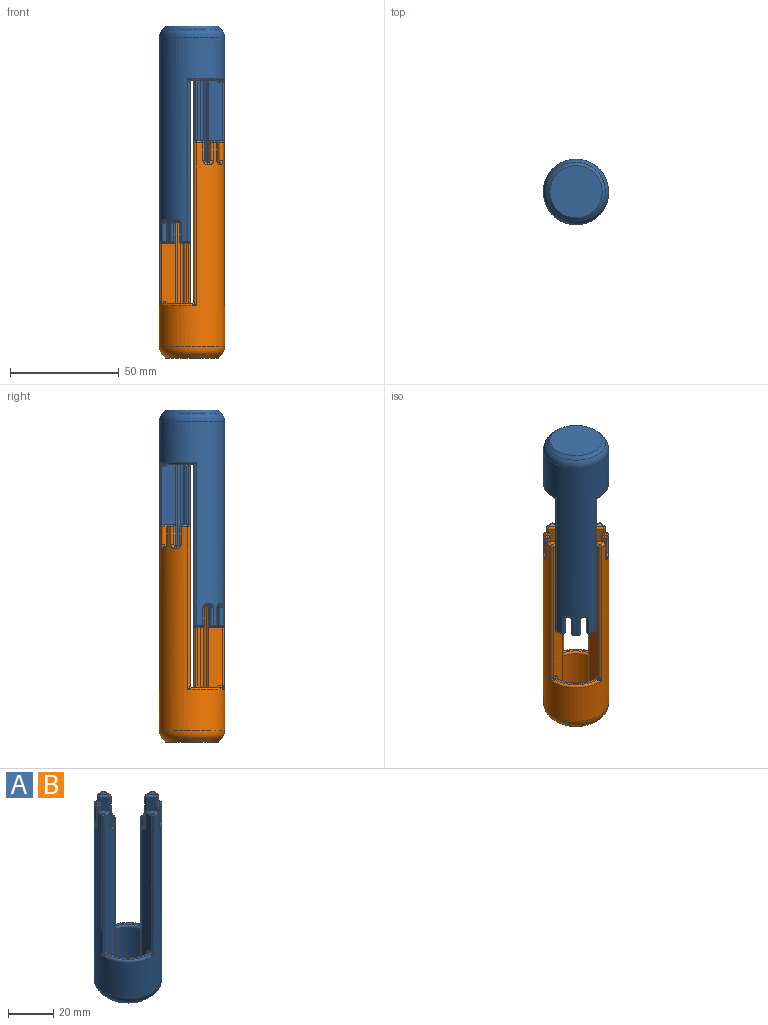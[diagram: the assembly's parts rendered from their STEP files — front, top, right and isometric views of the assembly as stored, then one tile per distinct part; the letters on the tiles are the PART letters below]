
ASSEMBLY  parts=2 mates=1
PART A: 263 faces, bbox 32.5x32.5x100 mm
  f0: cone r=12.88mm half-angle=45deg, axis (0,0,1), area 17.4mm2, adj f4,f217,f223,f235,f236,f237
  f1: cylinder r=12mm len=94mm, axis (0,0,1), area 703.3mm2, adj f26,f27,f166,f168,f170,f172,f176,f180
  f2: cylinder r=12mm len=19.76mm, axis (0,0,1), area 361.6mm2, adj f5,f228,f232,f234
  f3: plane 19.7x19.7mm, normal (0,0,1), area 194.3mm2, adj f235,f236,f237,f238,f239,f240,f241,f242
  f4: cylinder r=12mm len=19.76mm, axis (0,0,1), area 361.6mm2, adj f0,f217,f221,f223
  f5: cone r=12.88mm half-angle=45deg, axis (0,0,1), area 17.4mm2, adj f2,f228,f234,f260,f261,f262
  f6: cylinder r=12mm len=94mm, axis (0,0,1), area 703.3mm2, adj f28,f29,f103,f105,f107,f109,f113,f117
  f7: plane 1.63x1.25mm, normal (0,0,1), area 1mm2, adj f80,f84,f105,f112
  f8: plane 0.66x0.66mm, normal (0,0,1), area 0.2mm2, adj f73,f138,f142
  f9: plane 0.66x0.66mm, normal (0,0,1), area 0.2mm2, adj f67,f151,f152
  f10: plane 1.63x1.25mm, normal (0,0,1), area 1mm2, adj f57,f58,f184,f193
  f11: cylinder r=15mm len=93.93mm, axis (0,0,-1), area 4539.2mm2, adj f37,f38,f39,f40,f41,f42,f44,f104
  f12: plane 3.66x2.95mm, normal (0,0,1), area 5.6mm2, adj f63,f202,f206
  f13: plane 2.12x2.12mm, normal (0,0,1), area 2mm2, adj f62,f70,f176,f185
  f14: plane 3.66x2.95mm, normal (0,0,1), area 5.6mm2, adj f71,f136,f141
  f15: plane 2.12x2.12mm, normal (0,0,1), area 2mm2, adj f72,f78,f113,f120
  f16: plane 94x6.14mm, normal (0,-1,0), area 493.6mm2, adj f37,f206,f208,f211,f212,f216,f217,f219
  f17: plane 94x6.14mm, normal (-1,0,0), area 493.6mm2, adj f38,f141,f144,f146,f148,f220,f222,f223
  f18: plane 84.01x1mm, normal (0,-1,0), area 84mm2, adj f149,f152,f154,f155,f256
  f19: plane 84.31x2.17mm, normal (-1,0,0), area 182.6mm2, adj f26,f149,f151,f153,f252
  f20: plane 84.31x2.17mm, normal (0,1,0), area 182.6mm2, adj f27,f198,f200,f201,f244
  f21: plane 84.01x1mm, normal (1,0,0), area 84mm2, adj f201,f205,f207,f208,f240
  f22: plane 84.01x1mm, normal (0,1,0), area 84mm2, adj f137,f142,f144,f145,f241
  f23: plane 84.31x2.17mm, normal (1,0,0), area 182.6mm2, adj f28,f135,f137,f138,f245
  f24: plane 84.31x2.17mm, normal (0,-1,0), area 182.6mm2, adj f29,f85,f88,f91,f253
  f25: plane 84.01x1mm, normal (-1,0,0), area 84mm2, adj f85,f87,f89,f90,f257
  f26: cylinder r=1mm len=84.59mm, axis (0,0,1), area 170.4mm2, adj f1,f19,f156,f158,f160,f164,f250
  f27: cylinder r=1mm len=84.59mm, axis (0,0,1), area 170.4mm2, adj f1,f20,f188,f192,f194,f196,f246
  f28: cylinder r=1mm len=84.59mm, axis (0,0,1), area 170.4mm2, adj f6,f23,f125,f129,f131,f133,f247
  f29: cylinder r=1mm len=84.59mm, axis (0,0,1), area 170.4mm2, adj f6,f24,f93,f95,f97,f101,f251
  f30: plane 13.75x13.75mm, normal (0,0,1), area 20.7mm2, adj f39,f214,f216,f218,f220,f221
  f31: plane 3.66x2.95mm, normal (0,0,1), area 5.6mm2, adj f69,f165,f169
  f32: plane 3.66x2.95mm, normal (0,0,1), area 5.6mm2, adj f79,f100,f104
  f33: plane 24x24mm, normal (0,0,-1), area 452.4mm2, adj f43
  f34: plane 13.75x13.75mm, normal (0,0,1), area 20.7mm2, adj f42,f225,f227,f229,f231,f232
  f35: plane 94x6.14mm, normal (1,0,0), area 493.6mm2, adj f41,f154,f159,f161,f165,f231,f233,f234
  f36: plane 94x6.14mm, normal (0,1,0), area 493.6mm2, adj f40,f90,f94,f96,f100,f227,f228,f230
  f37: cylinder r=1mm len=75mm, axis (0,0,-1), area 125mm2, adj f11,f16,f204,f213,f214
  f38: cylinder r=1mm len=75mm, axis (0,0,-1), area 125mm2, adj f11,f17,f139,f215,f218
  f39: torus R=14mm, axis (0,0,1), area 38.6mm2, adj f11,f30,f213,f215
  f40: cylinder r=1mm len=75mm, axis (0,0,-1), area 125mm2, adj f11,f36,f102,f224,f225
  f41: cylinder r=1mm len=75mm, axis (0,0,-1), area 125mm2, adj f11,f35,f167,f226,f229
  f42: torus R=14mm, axis (0,0,1), area 38.6mm2, adj f11,f34,f224,f226
  f43: cone r=15mm half-angle=45deg, axis (0,0,1), area 174.2mm2, adj f33,f44
  f44: torus R=10mm, axis (0,0,-1), area 357.8mm2, adj f11,f43
  f45: plane 0.66x0.66mm, normal (0,0,1), area 0.2mm2, adj f81,f87,f88
  f46: plane 8x0.71mm, normal (0.71,0.71,0), area 8mm2, adj f78,f80,f109,f116
  f47: plane 8.25x2.95mm, normal (-0.71,-0.71,0), area 33.6mm2, adj f79,f81,f82,f83,f84,f96,f108
  f48: plane 1.63x1.25mm, normal (0,0,1), area 1mm2, adj f76,f77,f121,f128
  f49: plane 8x0.71mm, normal (-0.71,-0.71,0), area 8mm2, adj f72,f77,f117,f124
  f50: plane 8.25x2.95mm, normal (0.71,0.71,0), area 33.6mm2, adj f71,f73,f74,f75,f76,f132,f146
  f51: plane 8.25x2.95mm, normal (0.71,0.71,0), area 33.6mm2, adj f58,f59,f60,f61,f63,f197,f211
  f52: plane 8x0.71mm, normal (-0.71,-0.71,0), area 8mm2, adj f57,f62,f180,f189
  f53: plane 0.66x0.66mm, normal (0,0,1), area 0.2mm2, adj f61,f200,f205
  f54: plane 8.25x2.95mm, normal (-0.71,-0.71,0), area 33.6mm2, adj f64,f65,f66,f67,f69,f161,f173
  f55: plane 8x0.71mm, normal (0.71,0.71,0), area 8mm2, adj f68,f70,f172,f181
  f56: plane 1.63x1.25mm, normal (0,0,1), area 1mm2, adj f64,f68,f168,f177
  f57: cylinder r=1mm len=1.64mm, axis (-0.71,0.71,0), area 1.6mm2, adj f10,f52,f182,f191
  f58: cylinder r=1mm len=2.19mm, axis (0.71,-0.71,0), area 2.1mm2, adj f10,f51,f59,f186,f188,f195
  f59: bspline ~1.93x1.86mm, area 1mm2, adj f51,f58,f60,f190,f192
  f60: bspline ~1.47x1.03mm, area 0.5mm2, adj f51,f59,f61,f194
  f61: cylinder r=1mm len=2.54mm, axis (0.71,-0.71,0), area 1.9mm2, adj f51,f53,f60,f196,f198,f207,f212
  f62: cylinder r=1mm len=1.42mm, axis (0.71,-0.71,0), area 1.6mm2, adj f13,f52,f178,f187
  f63: cylinder r=1mm len=3.66mm, axis (-0.71,0.71,0), area 6.6mm2, adj f12,f51,f199,f209
  f64: cylinder r=1mm len=2.19mm, axis (-0.71,0.71,0), area 2.1mm2, adj f54,f56,f65,f164,f166,f175
  f65: bspline ~1.96x1.9mm, area 1mm2, adj f54,f64,f66,f160,f162
  f66: bspline ~1.47x1.03mm, area 0.5mm2, adj f54,f65,f67,f158
  f67: cylinder r=1mm len=2.54mm, axis (-0.71,0.71,0), area 1.9mm2, adj f9,f54,f66,f153,f155,f156,f159
  f68: cylinder r=1mm len=1.64mm, axis (0.71,-0.71,0), area 1.6mm2, adj f55,f56,f170,f179
  f69: cylinder r=1mm len=3.66mm, axis (0.71,-0.71,0), area 6.6mm2, adj f31,f54,f163,f171
  f70: cylinder r=1mm len=1.42mm, axis (-0.71,0.71,0), area 1.6mm2, adj f13,f55,f174,f183
  f71: cylinder r=1mm len=3.66mm, axis (-0.71,0.71,0), area 6.6mm2, adj f14,f50,f134,f143
  f72: cylinder r=1mm len=1.42mm, axis (0.71,-0.71,0), area 1.6mm2, adj f15,f49,f115,f122
  f73: cylinder r=1mm len=2.54mm, axis (0.71,-0.71,0), area 1.9mm2, adj f8,f50,f74,f133,f135,f145,f148
  f74: bspline ~1.55x1.18mm, area 0.5mm2, adj f50,f73,f75,f131
  f75: bspline ~1.9x1.79mm, area 1mm2, adj f50,f74,f76,f127,f129
  f76: cylinder r=1mm len=2.19mm, axis (0.71,-0.71,0), area 2.1mm2, adj f48,f50,f75,f123,f125,f130
  f77: cylinder r=1mm len=1.64mm, axis (-0.71,0.71,0), area 1.6mm2, adj f48,f49,f119,f126
  f78: cylinder r=1mm len=1.42mm, axis (-0.71,0.71,0), area 1.6mm2, adj f15,f46,f111,f118
  f79: cylinder r=1mm len=3.66mm, axis (0.71,-0.71,0), area 6.6mm2, adj f32,f47,f98,f106
  f80: cylinder r=1mm len=1.64mm, axis (0.71,-0.71,0), area 1.6mm2, adj f7,f46,f107,f114
  f81: cylinder r=1mm len=2.54mm, axis (-0.71,0.71,0), area 1.9mm2, adj f45,f47,f82,f89,f91,f93,f94
  f82: bspline ~1.55x1.18mm, area 0.5mm2, adj f47,f81,f83,f95
  f83: bspline ~1.93x1.86mm, area 1mm2, adj f47,f82,f84,f97,f99
  f84: cylinder r=1mm len=2.19mm, axis (-0.71,0.71,0), area 2.1mm2, adj f7,f47,f83,f101,f103,f110
  f85: cylinder r=1mm len=84mm, axis (0,0,1), area 131.9mm2, adj f24,f25,f86,f255
  f86: sphere r=1mm, area 1.6mm2, adj f85,f87,f88
  f87: cylinder r=1mm len=1mm, axis (0,1,0), area 1mm2, adj f25,f45,f86,f89
  f88: cylinder r=1mm len=1mm, axis (-1,0,0), area 1mm2, adj f24,f45,f86,f91
  f89: bspline ~1.01x1mm, area 0.4mm2, adj f25,f81,f87,f92
  f90: cylinder r=1mm len=84.01mm, axis (0,0,1), area 132mm2, adj f25,f36,f92,f259
  f91: bspline ~1.51x1.16mm, area 1.8mm2, adj f24,f81,f88,f93
  f92: sphere r=1mm, area 1.8mm2, adj f89,f90,f94
  f93: bspline ~1.18x1.02mm, area 0.3mm2, adj f29,f81,f91,f95
  f94: bspline ~2.95x2.35mm, area 4.9mm2, adj f36,f81,f92,f96
  f95: bspline ~0.76x0.56mm, area 0.2mm2, adj f29,f82,f93,f97
  f96: cylinder r=1mm len=8mm, axis (0,0,1), area 18.8mm2, adj f36,f47,f94,f98
  f97: bspline ~1.01x1mm, area 0.7mm2, adj f29,f83,f95,f99
  f98: sphere r=1mm, area 1.6mm2, adj f79,f96,f100
  f99: bspline ~0.72x0.45mm, area 0.1mm2, adj f83,f97,f101
  f100: cylinder r=1mm len=3.66mm, axis (-1,0,0), area 5.7mm2, adj f32,f36,f98,f102
  f101: bspline ~1.41x1.33mm, area 1.1mm2, adj f29,f84,f99,f103
  f102: sphere r=1mm, area 1.7mm2, adj f40,f100,f104
  f103: bspline ~1.4x1.17mm, area 0.4mm2, adj f6,f84,f101,f105
  f104: torus R=14mm, axis (0,0,1), area 5mm2, adj f11,f32,f102,f106
  f105: torus R=13mm, axis (0,0,1), area 1.6mm2, adj f6,f7,f103,f107
  f106: sphere r=1mm, area 1.3mm2, adj f79,f104,f108
  f107: bspline ~2.44x2.03mm, area 3.4mm2, adj f6,f80,f105,f109
  f108: cylinder r=1mm len=8mm, axis (0,0,-1), area 16.1mm2, adj f11,f47,f106,f110
  f109: cylinder r=1mm len=8mm, axis (0,0,1), area 13.2mm2, adj f6,f46,f107,f111
  f110: bspline ~2.53x2.42mm, area 4.1mm2, adj f11,f84,f108,f112
  f111: sphere r=1mm, area 1.1mm2, adj f78,f109,f113
  f112: torus R=14mm, axis (0,0,1), area 1.7mm2, adj f7,f11,f110,f114
  f113: torus R=13mm, axis (0,0,1), area 3mm2, adj f6,f15,f111,f115
  f114: bspline ~2.51x2.11mm, area 3.4mm2, adj f11,f80,f112,f116
  f115: sphere r=1mm, area 1.1mm2, adj f72,f113,f117
  f116: cylinder r=1mm len=8mm, axis (0,0,-1), area 12mm2, adj f11,f46,f114,f118
  f117: cylinder r=1mm len=8mm, axis (0,0,1), area 13.2mm2, adj f6,f49,f115,f119
  f118: sphere r=1mm, area 2.1mm2, adj f78,f116,f120
  f119: bspline ~2.44x2.03mm, area 3.4mm2, adj f6,f77,f117,f121
  f120: torus R=14mm, axis (0,0,1), area 3.3mm2, adj f11,f15,f118,f122
  f121: torus R=13mm, axis (0,0,1), area 1.6mm2, adj f6,f48,f119,f123
  f122: sphere r=1mm, area 0.9mm2, adj f72,f120,f124
  f123: bspline ~1.14x1.1mm, area 0.4mm2, adj f6,f76,f121,f125
  f124: cylinder r=1mm len=8mm, axis (0,0,-1), area 12mm2, adj f11,f49,f122,f126
  f125: bspline ~1.41x1.33mm, area 1.1mm2, adj f28,f76,f123,f127
  f126: bspline ~2.51x2.44mm, area 3.4mm2, adj f11,f77,f124,f128
  f127: bspline ~0.72x0.45mm, area 0.1mm2, adj f75,f125,f129
  f128: torus R=14mm, axis (0,0,1), area 1.7mm2, adj f11,f48,f126,f130
  f129: bspline ~1.05x1.04mm, area 0.7mm2, adj f28,f75,f127,f131
  f130: bspline ~2.53x2.11mm, area 4.1mm2, adj f11,f76,f128,f132
  f131: bspline ~0.78x0.61mm, area 0.2mm2, adj f28,f74,f129,f133
  f132: cylinder r=1mm len=8mm, axis (0,0,-1), area 16.1mm2, adj f11,f50,f130,f134
  f133: bspline ~1.18x1.02mm, area 0.3mm2, adj f28,f73,f131,f135
  f134: sphere r=1mm, area 2.5mm2, adj f71,f132,f136
  f135: bspline ~1.51x1.16mm, area 1.8mm2, adj f23,f73,f133,f138
  f136: torus R=14mm, axis (0,0,1), area 5mm2, adj f11,f14,f134,f139
  f137: cylinder r=1mm len=84mm, axis (0,0,1), area 131.9mm2, adj f22,f23,f140,f243
  f138: cylinder r=1mm len=1mm, axis (0,-1,0), area 1mm2, adj f8,f23,f135,f140
  f139: sphere r=1mm, area 1.7mm2, adj f38,f136,f141
  f140: sphere r=1mm, area 2.1mm2, adj f137,f138,f142
  f141: cylinder r=1mm len=3.66mm, axis (0,-1,0), area 5.7mm2, adj f14,f17,f139,f143
  f142: cylinder r=1mm len=1mm, axis (1,0,0), area 1mm2, adj f8,f22,f140,f145
  f143: sphere r=1mm, area 1.6mm2, adj f71,f141,f146
  f144: cylinder r=1mm len=84.01mm, axis (0,0,1), area 132mm2, adj f17,f22,f147,f239
  f145: bspline ~1.01x1mm, area 0.4mm2, adj f22,f73,f142,f147
  f146: cylinder r=1mm len=8mm, axis (0,0,-1), area 18.8mm2, adj f17,f50,f143,f148
  f147: sphere r=1mm, area 1.8mm2, adj f144,f145,f148
  f148: bspline ~2.95x2.35mm, area 4.9mm2, adj f17,f73,f146,f147
  f149: cylinder r=1mm len=84mm, axis (0,0,1), area 131.9mm2, adj f18,f19,f150,f254
  f150: sphere r=1mm, area 1.6mm2, adj f149,f151,f152
  f151: cylinder r=1mm len=1mm, axis (0,1,0), area 1mm2, adj f9,f19,f150,f153
  f152: cylinder r=1mm len=1mm, axis (-1,0,0), area 1mm2, adj f9,f18,f150,f155
  f153: bspline ~1.51x1.16mm, area 1.8mm2, adj f19,f67,f151,f156
  f154: cylinder r=1mm len=84.01mm, axis (0,0,-1), area 132mm2, adj f18,f35,f157,f258
  f155: bspline ~1.01x1mm, area 0.4mm2, adj f18,f67,f152,f157
  f156: bspline ~1.18x1.02mm, area 0.3mm2, adj f26,f67,f153,f158
  f157: sphere r=1mm, area 1.8mm2, adj f154,f155,f159
  f158: bspline ~0.76x0.56mm, area 0.2mm2, adj f26,f66,f156,f160
  f159: bspline ~2.95x2.35mm, area 4.9mm2, adj f35,f67,f157,f161
  f160: bspline ~1.03x1.03mm, area 0.7mm2, adj f26,f65,f158,f162
  f161: cylinder r=1mm len=8mm, axis (0,0,-1), area 18.8mm2, adj f35,f54,f159,f163
  f162: bspline ~0.72x0.45mm, area 0mm2, adj f65,f160,f164
  f163: sphere r=1mm, area 2.7mm2, adj f69,f161,f165
  f164: bspline ~1.41x1.33mm, area 1.1mm2, adj f26,f64,f162,f166
  f165: cylinder r=1mm len=3.66mm, axis (0,1,0), area 5.7mm2, adj f31,f35,f163,f167
  f166: bspline ~1.14x1.1mm, area 0.4mm2, adj f1,f64,f164,f168
  f167: sphere r=1mm, area 1.1mm2, adj f41,f165,f169
  f168: torus R=13mm, axis (0,0,1), area 1.6mm2, adj f1,f56,f166,f170
  f169: torus R=14mm, axis (0,0,1), area 5mm2, adj f11,f31,f167,f171
  f170: bspline ~2.44x2.03mm, area 3.4mm2, adj f1,f68,f168,f172
  f171: sphere r=1mm, area 2.5mm2, adj f69,f169,f173
  f172: cylinder r=1mm len=8mm, axis (0,0,1), area 13.2mm2, adj f1,f55,f170,f174
  f173: cylinder r=1mm len=8mm, axis (0,0,-1), area 16.1mm2, adj f11,f54,f171,f175
  f174: sphere r=1mm, area 1.1mm2, adj f70,f172,f176
  f175: bspline ~2.53x2.11mm, area 4.1mm2, adj f11,f64,f173,f177
  f176: torus R=13mm, axis (0,0,1), area 3mm2, adj f1,f13,f174,f178
  f177: torus R=14mm, axis (0,0,1), area 1.7mm2, adj f11,f56,f175,f179
  f178: sphere r=1mm, area 1.1mm2, adj f62,f176,f180
  f179: bspline ~2.51x2.44mm, area 3.4mm2, adj f11,f68,f177,f181
  f180: cylinder r=1mm len=8mm, axis (0,0,1), area 13.2mm2, adj f1,f52,f178,f182
  f181: cylinder r=1mm len=8mm, axis (0,0,-1), area 12mm2, adj f11,f55,f179,f183
  f182: bspline ~2.44x2.03mm, area 3.4mm2, adj f1,f57,f180,f184
  f183: sphere r=1mm, area 0.9mm2, adj f70,f181,f185
  f184: torus R=13mm, axis (0,0,1), area 1.6mm2, adj f1,f10,f182,f186
  f185: torus R=14mm, axis (0,0,1), area 3.3mm2, adj f11,f13,f183,f187
  f186: bspline ~1.4x1.17mm, area 0.4mm2, adj f1,f58,f184,f188
  f187: sphere r=1mm, area 2.1mm2, adj f62,f185,f189
  f188: bspline ~1.41x1.33mm, area 1.1mm2, adj f27,f58,f186,f190
  f189: cylinder r=1mm len=8mm, axis (0,0,-1), area 12mm2, adj f11,f52,f187,f191
  f190: bspline ~0.72x0.45mm, area 0.1mm2, adj f59,f188,f192
  f191: bspline ~2.51x2.11mm, area 3.4mm2, adj f11,f57,f189,f193
  f192: bspline ~1.04x1.04mm, area 1.9mm2, adj f27,f59,f190,f194
  f193: torus R=14mm, axis (0,0,1), area 1.7mm2, adj f10,f11,f191,f195
  f194: bspline ~0.78x0.61mm, area 0.2mm2, adj f27,f60,f192,f196
  f195: bspline ~2.53x2.42mm, area 4.1mm2, adj f11,f58,f193,f197
  f196: bspline ~1.18x1.02mm, area 0.3mm2, adj f27,f61,f194,f198
  f197: cylinder r=1mm len=8mm, axis (0,0,-1), area 16.1mm2, adj f11,f51,f195,f199
  f198: bspline ~1.51x1.16mm, area 1.8mm2, adj f20,f61,f196,f200
  f199: sphere r=1mm, area 1.3mm2, adj f63,f197,f202
  f200: cylinder r=1mm len=1mm, axis (1,0,0), area 1mm2, adj f20,f53,f198,f203
  f201: cylinder r=1mm len=84mm, axis (0,0,1), area 131.9mm2, adj f20,f21,f203,f242
  f202: torus R=14mm, axis (0,0,1), area 5mm2, adj f11,f12,f199,f204
  f203: sphere r=1mm, area 1mm2, adj f200,f201,f205
  f204: sphere r=1mm, area 1.7mm2, adj f37,f202,f206
  f205: cylinder r=1mm len=1mm, axis (0,-1,0), area 1mm2, adj f21,f53,f203,f207
  f206: cylinder r=1mm len=3.66mm, axis (1,0,0), area 5.7mm2, adj f12,f16,f204,f209
  f207: bspline ~1.01x1mm, area 0.4mm2, adj f21,f61,f205,f210
  f208: cylinder r=1mm len=84.01mm, axis (0,0,-1), area 132mm2, adj f16,f21,f210,f238
  f209: sphere r=1mm, area 2.7mm2, adj f63,f206,f211
  f210: sphere r=1mm, area 1.6mm2, adj f207,f208,f212
  f211: cylinder r=1mm len=8mm, axis (0,0,1), area 18.8mm2, adj f16,f51,f209,f212
  f212: bspline ~2.95x2.35mm, area 4.9mm2, adj f16,f61,f210,f211
  f213: bspline ~2.13x2mm, area 1.2mm2, adj f37,f39,f214
  f214: torus R=2mm, axis (0,0,1), area 0.1mm2, adj f30,f37,f213,f216
  f215: bspline ~2.13x2mm, area 1.2mm2, adj f38,f39,f218
  f216: cylinder r=1mm len=1mm, axis (-1,0,0), area 1.4mm2, adj f16,f30,f214,f219
  f217: cylinder r=1mm len=20.04mm, axis (0,0,1), area 31.4mm2, adj f0,f4,f16,f219,f236
  f218: torus R=2mm, axis (0,0,1), area 0.1mm2, adj f30,f38,f215,f220
  f219: bspline ~2.45x2.34mm, area 3.4mm2, adj f16,f216,f217,f221
  f220: cylinder r=1mm len=1mm, axis (0,1,0), area 1.4mm2, adj f17,f30,f218,f222
  f221: torus R=13mm, axis (0,0,1), area 29.7mm2, adj f4,f30,f219,f222
  f222: bspline ~2.45x2.34mm, area 3.4mm2, adj f17,f220,f221,f223
  f223: cylinder r=1mm len=20.04mm, axis (0,0,1), area 31.4mm2, adj f0,f4,f17,f222,f237
  f224: bspline ~2.13x2mm, area 1.2mm2, adj f40,f42,f225
  f225: torus R=2mm, axis (0,0,1), area 0.1mm2, adj f34,f40,f224,f227
  f226: bspline ~2.13x2mm, area 1.2mm2, adj f41,f42,f229
  f227: cylinder r=1mm len=1mm, axis (1,0,0), area 1.4mm2, adj f34,f36,f225,f230
  f228: cylinder r=1mm len=20.04mm, axis (0,0,1), area 31.4mm2, adj f2,f5,f36,f230,f261
  f229: torus R=2mm, axis (0,0,1), area 0.1mm2, adj f34,f41,f226,f231
  f230: bspline ~2.45x2.34mm, area 3.4mm2, adj f36,f227,f228,f232
  f231: cylinder r=1mm len=1mm, axis (0,-1,0), area 1.4mm2, adj f34,f35,f229,f233
  f232: torus R=13mm, axis (0,0,1), area 29.7mm2, adj f2,f34,f230,f233
  f233: bspline ~2.45x2.34mm, area 3.4mm2, adj f35,f231,f232,f234
  f234: cylinder r=1mm len=20.04mm, axis (0,0,1), area 31.4mm2, adj f2,f5,f35,f233,f260
  f235: torus R=9.93mm, axis (0,0,1), area 24.5mm2, adj f0,f3,f236,f237
  f236: cylinder r=2mm len=3.96mm, axis (1,0,0), area 10.2mm2, adj f0,f3,f16,f217,f235,f238
  f237: cylinder r=2mm len=3.96mm, axis (0,-1,0), area 10.2mm2, adj f0,f3,f17,f223,f235,f239
  f238: torus R=3mm, axis (0,0,1), area 8.5mm2, adj f3,f208,f236,f240
  f239: torus R=3mm, axis (0,0,1), area 8.5mm2, adj f3,f144,f237,f241
  f240: cylinder r=2mm len=2mm, axis (0,1,0), area 3.1mm2, adj f3,f21,f238,f242
  f241: cylinder r=2mm len=2mm, axis (-1,0,0), area 3.1mm2, adj f3,f22,f239,f243
  f242: torus R=3mm, axis (0,0,1), area 8.5mm2, adj f3,f201,f240,f244
  f243: torus R=3mm, axis (0,0,1), area 8.5mm2, adj f3,f137,f241,f245
  f244: cylinder r=2mm len=2.17mm, axis (-1,0,0), area 4.9mm2, adj f3,f20,f242,f246
  f245: cylinder r=2mm len=2.17mm, axis (0,1,0), area 4.9mm2, adj f3,f23,f243,f247
  f246: bspline ~3.33x2.14mm, area 3.4mm2, adj f27,f244,f248
  f247: bspline ~3.33x2.14mm, area 3.4mm2, adj f28,f245,f249
  f248: torus R=10mm, axis (0,0,1), area 18.3mm2, adj f1,f3,f246,f250
  f249: torus R=10mm, axis (0,0,1), area 18.3mm2, adj f3,f6,f247,f251
  f250: bspline ~3.33x2.14mm, area 3.4mm2, adj f26,f248,f252
  f251: bspline ~3.33x2.14mm, area 3.4mm2, adj f29,f249,f253
  f252: cylinder r=2mm len=2.17mm, axis (0,-1,0), area 4.9mm2, adj f3,f19,f250,f254
  f253: cylinder r=2mm len=2.17mm, axis (1,0,0), area 4.9mm2, adj f3,f24,f251,f255
  f254: torus R=3mm, axis (0,0,1), area 8.5mm2, adj f3,f149,f252,f256
  f255: torus R=3mm, axis (0,0,1), area 8.5mm2, adj f3,f85,f253,f257
  f256: cylinder r=2mm len=2mm, axis (1,0,0), area 3.1mm2, adj f3,f18,f254,f258
  f257: cylinder r=2mm len=2mm, axis (0,-1,0), area 3.1mm2, adj f3,f25,f255,f259
  f258: torus R=3mm, axis (0,0,1), area 8.5mm2, adj f3,f154,f256,f260
  f259: torus R=3mm, axis (0,0,1), area 8.5mm2, adj f3,f90,f257,f261
  f260: cylinder r=2mm len=3.96mm, axis (0,1,0), area 10.2mm2, adj f3,f5,f35,f234,f258,f262
  f261: cylinder r=2mm len=3.96mm, axis (-1,0,0), area 10.2mm2, adj f3,f5,f36,f228,f259,f262
  f262: torus R=9.93mm, axis (0,0,1), area 24.5mm2, adj f3,f5,f260,f261
PART B: same geometry as A
PLACE A rot(axis=(0,1,0),180deg) t=(-29.53,-75.48,133.42)mm
PLACE B t=(-29.53,-75.48,-19.36)mm fixed
MATE slider A.f0 <-> B.f0  axis (0,0,1) through (-29.53,-75.48,133.42)mm
